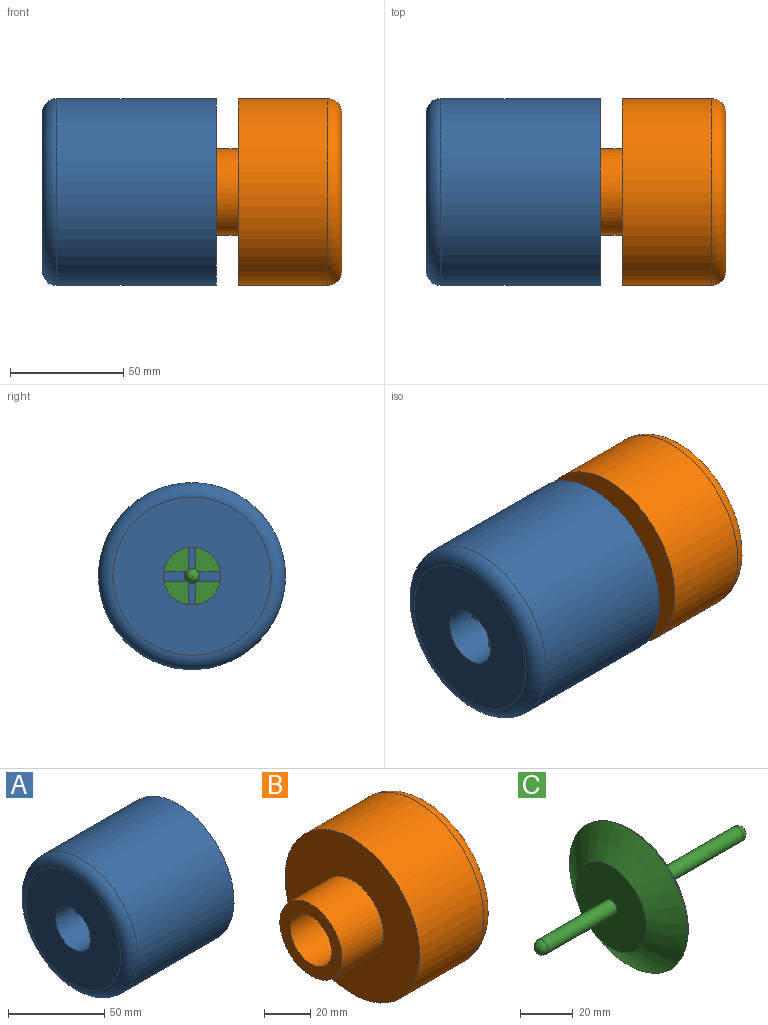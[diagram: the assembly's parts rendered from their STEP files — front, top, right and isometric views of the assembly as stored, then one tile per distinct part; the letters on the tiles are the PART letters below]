
ASSEMBLY  parts=3 mates=2
PART A: 29 faces, bbox 76.9x89.4x89.4 mm
  f0: plane 10.17x4.45mm, normal (-1,0,0), area 42.4mm2, adj f4,f20,f21,f27
  f1: plane 9.74x3.23mm, normal (-1,0,0), area 30.4mm2, adj f5,f20,f26,f28
  f2: plane 10.17x4.45mm, normal (-1,0,0), area 42.4mm2, adj f6,f20,f23,f25
  f3: plane 9.74x3.23mm, normal (-1,0,0), area 30.4mm2, adj f10,f20,f22,f24
  f4: cylinder r=3.37mm len=4.45mm, axis (-1,0,0), area 15.4mm2, adj f0,f7,f21,f27
  f5: cylinder r=3.37mm len=3.23mm, axis (-1,0,0), area 10.7mm2, adj f1,f8,f26,f28
  f6: cylinder r=3.37mm len=4.45mm, axis (-1,0,0), area 15.4mm2, adj f2,f9,f23,f25
  f7: cone r=3.37mm half-angle=80.3deg, axis (1,0,0), area 43mm2, adj f4,f20,f21,f27
  f8: cone r=3.37mm half-angle=80.3deg, axis (1,0,0), area 30.9mm2, adj f5,f20,f26,f28
  f9: cone r=3.37mm half-angle=80.3deg, axis (1,0,0), area 43mm2, adj f6,f20,f23,f25
  f10: cylinder r=3.37mm len=3.23mm, axis (-1,0,0), area 10.7mm2, adj f3,f11,f22,f24
  f11: cone r=3.37mm half-angle=80.3deg, axis (1,0,0), area 30.9mm2, adj f10,f20,f22,f24
  f12: plane 38.1x38.1mm, normal (1,0,0), area 633.4mm2, adj f13,f20
  f13: cylinder r=19.05mm len=38.1mm, axis (-1,0,0), area 1520.1mm2, adj f12,f14
  f14: plane 63.5x63.5mm, normal (1,0,0), area 2026.8mm2, adj f13,f15
  f15: cylinder r=31.75mm len=63.5mm, axis (-1,0,0), area 10134.1mm2, adj f14,f16
  f16: plane 82.55x82.55mm, normal (1,0,0), area 2185.2mm2, adj f15,f17
  f17: cylinder r=41.27mm len=82.55mm, axis (-1,0,0), area 18289.8mm2, adj f16,f18
  f18: torus R=34.92mm, axis (-1,0,0), area 2442.2mm2, adj f17,f19
  f19: plane 69.85x69.85mm, normal (-1,0,0), area 3325.3mm2, adj f18,f20
  f20: cylinder r=12.7mm len=38.77mm, axis (-1,0,0), area 3020.5mm2, adj f0,f1,f2,f3,f7,f8,f9,f11
  f21: plane 9.98x4.77mm, normal (0,0,1), area 39.4mm2, adj f0,f4,f7,f20
  f22: plane 9.64x4.77mm, normal (0,1,0), area 38.2mm2, adj f3,f10,f11,f20
  f23: plane 9.98x4.77mm, normal (0,0,1), area 39.4mm2, adj f2,f6,f9,f20
  f24: plane 9.64x4.77mm, normal (0,-1,0), area 38.2mm2, adj f3,f10,f11,f20
  f25: plane 9.98x4.77mm, normal (0,0,-1), area 39.4mm2, adj f2,f6,f9,f20
  f26: plane 9.64x4.77mm, normal (0,-1,0), area 38.2mm2, adj f1,f5,f8,f20
  f27: plane 9.98x4.77mm, normal (0,0,-1), area 39.4mm2, adj f0,f4,f7,f20
  f28: plane 9.64x4.77mm, normal (0,1,0), area 38.2mm2, adj f1,f5,f8,f20
PART B: 27 faces, bbox 71.1x89.4x89.4 mm
  f0: plane 10.14x4.45mm, normal (1,0,0), area 42.3mm2, adj f9,f18,f23,f25
  f1: plane 10.14x4.45mm, normal (1,0,0), area 42.3mm2, adj f8,f18,f20,f26
  f2: plane 10.14x4.45mm, normal (1,0,0), area 42.3mm2, adj f10,f18,f22,f24
  f3: plane 10.14x4.45mm, normal (1,0,0), area 42.3mm2, adj f11,f18,f19,f21
  f4: cone r=3.39mm half-angle=68.6deg, axis (-1,0,0), area 45.4mm2, adj f9,f18,f23,f25
  f5: cone r=3.39mm half-angle=68.6deg, axis (-1,0,0), area 45.4mm2, adj f8,f18,f20,f26
  f6: cone r=3.39mm half-angle=68.6deg, axis (-1,0,0), area 45.4mm2, adj f11,f18,f19,f21
  f7: cone r=3.39mm half-angle=68.6deg, axis (-1,0,0), area 45.4mm2, adj f10,f18,f22,f24
  f8: cylinder r=3.39mm len=4.45mm, axis (-1,0,0), area 15.4mm2, adj f1,f5,f20,f26
  f9: cylinder r=3.39mm len=4.45mm, axis (-1,0,0), area 15.4mm2, adj f0,f4,f23,f25
  f10: cylinder r=3.39mm len=4.45mm, axis (-1,0,0), area 15.4mm2, adj f2,f7,f22,f24
  f11: cylinder r=3.39mm len=4.45mm, axis (-1,0,0), area 15.4mm2, adj f3,f6,f19,f21
  f12: plane 69.85x69.85mm, normal (1,0,0), area 3325.3mm2, adj f13,f18
  f13: torus R=34.92mm, axis (-1,0,0), area 2442.2mm2, adj f12,f14
  f14: cylinder r=41.27mm len=82.55mm, axis (-1,0,0), area 10214.1mm2, adj f13,f15
  f15: plane 82.55x82.55mm, normal (-1,0,0), area 4212mm2, adj f14,f16
  f16: cylinder r=19.05mm len=38.1mm, axis (-1,0,0), area 3040.2mm2, adj f15,f17
  f17: plane 38.1x38.1mm, normal (-1,0,0), area 633.4mm2, adj f16,f18
  f18: cylinder r=12.7mm len=71.14mm, axis (-1,0,0), area 5554.3mm2, adj f0,f1,f2,f3,f4,f5,f6,f7
  f19: plane 9.95x6.83mm, normal (0,0,1), area 49.2mm2, adj f3,f6,f11,f18
  f20: plane 9.95x6.83mm, normal (0,-1,0), area 49.2mm2, adj f1,f5,f8,f18
  f21: plane 9.95x6.83mm, normal (0,0,-1), area 49.2mm2, adj f3,f6,f11,f18
  f22: plane 9.95x6.83mm, normal (0,-1,0), area 49.2mm2, adj f2,f7,f10,f18
  f23: plane 9.95x6.83mm, normal (0,0,-1), area 49.2mm2, adj f0,f4,f9,f18
  f24: plane 9.95x6.83mm, normal (0,1,0), area 49.2mm2, adj f2,f7,f10,f18
  f25: plane 9.95x6.83mm, normal (0,0,1), area 49.2mm2, adj f0,f4,f9,f18
  f26: plane 9.95x6.83mm, normal (0,1,0), area 49.2mm2, adj f1,f5,f8,f18
PART C: 11 faces, bbox 111.1x63.4x63.4 mm
  f0: plane 38.1x38.1mm, normal (-1,0,0), area 1108.4mm2, adj f1,f10
  f1: cylinder r=3.17mm len=36.87mm, axis (-1,0,0), area 735.5mm2, adj f0,f2
  f2: sphere r=3.17mm, area 63.3mm2, adj f1
  f3: sphere r=3.17mm, area 63.3mm2, adj f4
  f4: cylinder r=3.17mm len=58.46mm, axis (-1,0,0), area 1166.2mm2, adj f3,f5
  f5: plane 38.1x38.1mm, normal (1,0,0), area 1108.4mm2, adj f4,f6
  f6: cylinder r=19.05mm len=38.1mm, axis (-1,0,0), area 940mm2, adj f5,f7
  f7: cone r=31.01mm half-angle=53.5deg, axis (1,0,0), area 2340.3mm2, adj f6,f8
  f8: cone r=31.72mm half-angle=36.5deg, axis (-1,0,0), area 234mm2, adj f7,f9
  f9: cylinder r=31.72mm len=63.44mm, axis (-1,0,0), area 13.5mm2, adj f8,f10
  f10: cone r=19.05mm half-angle=53.5deg, axis (1,0,0), area 2513.4mm2, adj f0,f9
PLACE A at identity fixed
PLACE B t=(-2.06,0,0)mm
PLACE C t=(11.56,0,0)mm
MATE slider C.f1 <-> B.f4  axis (1,0,0) through (-73.19,0,0)mm
MATE fastened B.f4 <-> A.f4  axis (-1,0,0) through (-47.79,0,0)mm
